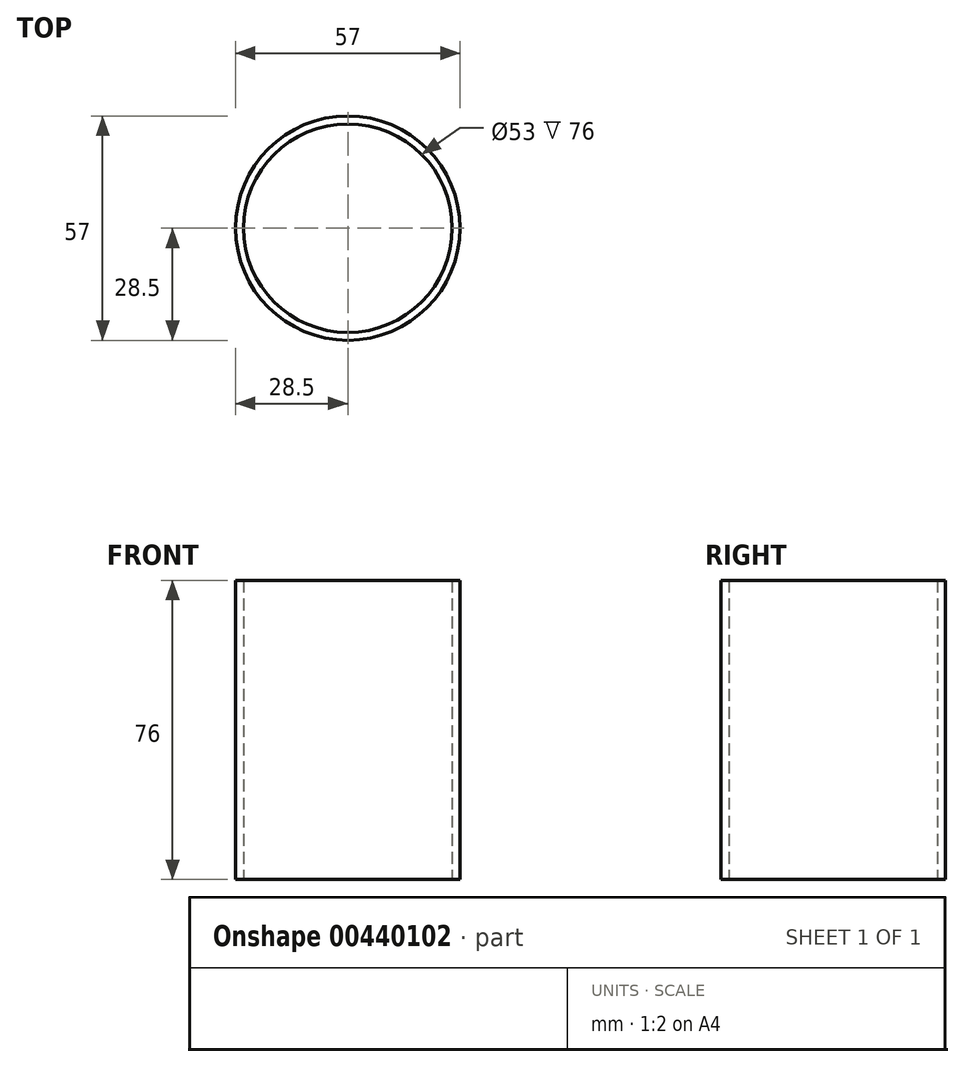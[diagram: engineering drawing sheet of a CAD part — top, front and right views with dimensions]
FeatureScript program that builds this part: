
annotation { "Feature Type Name" : "Feature", "Feature Type Description" : "" }
export const myFeature = defineFeature(function(context is Context, id is Id, definition is map)
    precondition{}
    {
        {
            var Q0;
            Q0=qCreatedBy(makeId("Top.planeOp"),FACE);
            var sketch = newSketch(context, id + "F0", { "sketchPlane" : qUnion([Q0])});
            skCircle(sketch, "E0", {"center": v(0, 0) * mm, "radius": 26.5 * mm});
            skCircle(sketch, "E1", {"center": v(0, 0) * mm, "radius": 28.5 * mm});
            skSolve(sketch);
        }
        {
            var Q0;
            Q0=makeQuery(id+"F0.imprint","IMPRINT",FACE,{"disambiguationData":[TD([[makeQuery(id+"F0.imprint","IMPRINT",EDGE,{"derivedFrom":sQuery(id+"F0.wireOp",EDGE,"E0")}),-1.0]])]});
            extrude(context, id + "F1", {"entities" : qUnion([Q0]), "depth" : 76 * mm, "offsetDistance" : 25 * mm});
        }
    });
